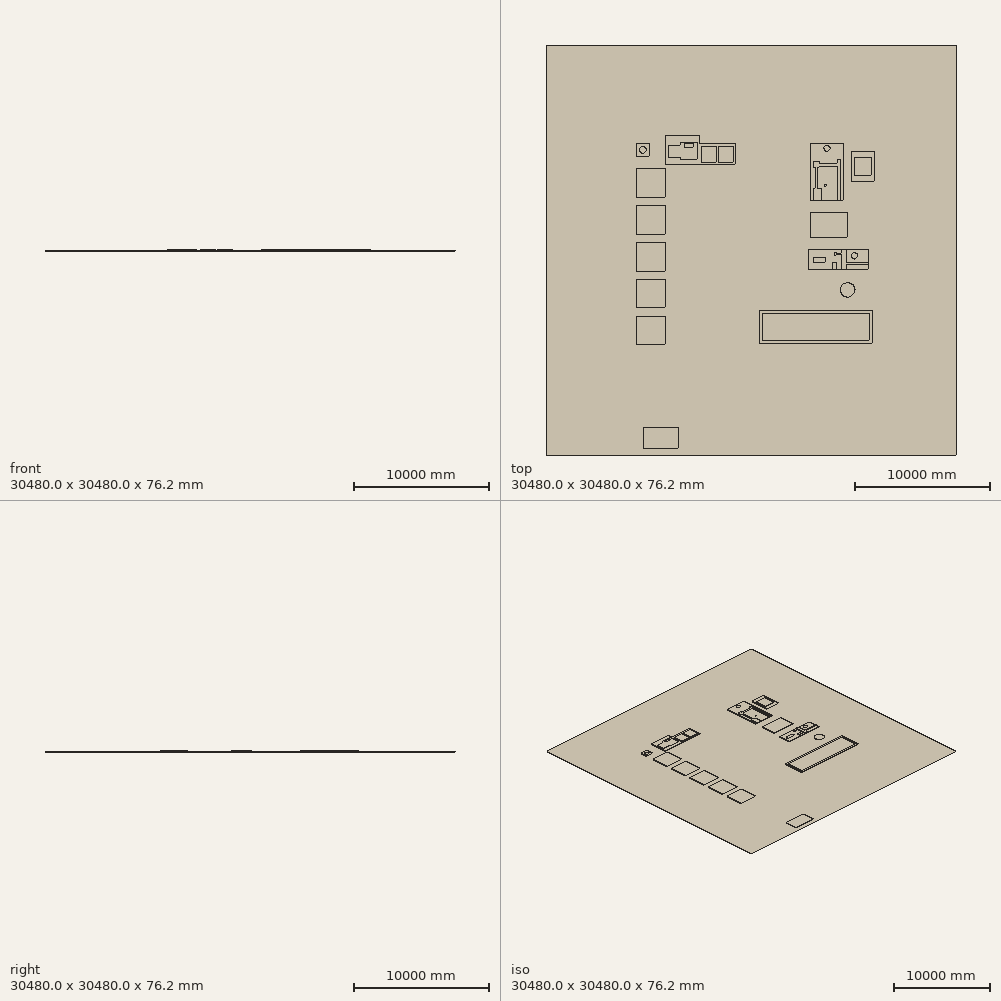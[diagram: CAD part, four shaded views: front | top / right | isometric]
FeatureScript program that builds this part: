
annotation { "Feature Type Name" : "Feature", "Feature Type Description" : "" }
export const myFeature = defineFeature(function(context is Context, id is Id, definition is map)
    precondition{}
    {
        {
            var Q0;
            Q0=qCreatedBy(makeId("Top.planeOp"),FACE);
            var sketch = newSketch(context, id + "F0", { "sketchPlane" : qUnion([Q0])});
            skLineSegment(sketch, "E0.bottom", {"start": v(15240, 15240) * mm, "end": v(-15240, 15240) * mm});
            skLineSegment(sketch, "E0.top", {"start": v(15240, -15240) * mm, "end": v(-15240, -15240) * mm});
            skLineSegment(sketch, "E0.left", {"start": v(15240, 15240) * mm, "end": v(15240, -15240) * mm});
            skLineSegment(sketch, "E0.right", {"start": v(-15240, 15240) * mm, "end": v(-15240, -15240) * mm});
            skPoint(sketch, "E0.middle", {"position": v(0, 0) * mm});
            skSolve(sketch);
        }
        {
            var Q0;
            Q0=qSketchRegion(id+"F0",true);
            extrude(context, id + "F1", {"entities" : qUnion([Q0]), "depth" : 25.4 * mm, "offsetDistance" : 25.4 * mm});
        }
        {
            var Q0;
            Q0=makeQuery(id+"F1.opExtrude","CAP_FACE",FACE,{"disambiguationData":[OSD([sQuery(id+"F0.wireOp",EDGE,"E0.bottom"),sQuery(id+"F0.wireOp",EDGE,"E0.top"),sQuery(id+"F0.wireOp",EDGE,"E0.left"),sQuery(id+"F0.wireOp",EDGE,"E0.right")])],"isStart":false});
            var sketch = newSketch(context, id + "F2", { "sketchPlane" : qUnion([Q0])});
            skLineSegment(sketch, "E1.bottom", {"start": v(-6400.8, 7975.6) * mm, "end": v(-1219.2, 7975.6) * mm});
            skLineSegment(sketch, "E1.top", {"start": v(-6400.8, 6400.8) * mm, "end": v(-1219.2, 6400.8) * mm});
            skLineSegment(sketch, "E1.left", {"start": v(-6400.8, 7975.6) * mm, "end": v(-6400.8, 6400.8) * mm});
            skLineSegment(sketch, "E1.right", {"start": v(-1219.2, 7975.6) * mm, "end": v(-1219.2, 6400.8) * mm});
            skLineSegment(sketch, "E2.bottom", {"start": v(-8534.4, 7924.8) * mm, "end": v(-7620, 7924.8) * mm});
            skLineSegment(sketch, "E2.top", {"start": v(-8534.4, 7010.4) * mm, "end": v(-7620, 7010.4) * mm});
            skLineSegment(sketch, "E2.left", {"start": v(-8534.4, 7924.8) * mm, "end": v(-8534.4, 7010.4) * mm});
            skLineSegment(sketch, "E2.right", {"start": v(-7620, 7924.8) * mm, "end": v(-7620, 7010.4) * mm});
            skCircle(sketch, "E3", {"center": v(-8077.2, 7467.6) * mm, "radius": 254 * mm});
            skLineSegment(sketch, "E4.bottom", {"start": v(4242.66, 50.8) * mm, "end": v(8687.66, 50.8) * mm});
            skLineSegment(sketch, "E4.top", {"start": v(4242.66, -1397) * mm, "end": v(8687.66, -1397) * mm});
            skLineSegment(sketch, "E4.left", {"start": v(4242.66, 50.8) * mm, "end": v(4242.66, -1397) * mm});
            skLineSegment(sketch, "E4.right", {"start": v(8687.66, 50.8) * mm, "end": v(8687.66, -1397) * mm});
            skCircle(sketch, "E5", {"center": v(7163.66, -2934.73) * mm, "radius": 533.4 * mm});
            skLineSegment(sketch, "E6.bottom", {"start": v(610.46, -4458.73) * mm, "end": v(8992.46, -4458.73) * mm});
            skLineSegment(sketch, "E6.top", {"start": v(610.46, -6897.13) * mm, "end": v(8992.46, -6897.13) * mm});
            skLineSegment(sketch, "E6.left", {"start": v(610.46, -4458.73) * mm, "end": v(610.46, -6897.13) * mm});
            skLineSegment(sketch, "E6.right", {"start": v(8992.46, -4458.73) * mm, "end": v(8992.46, -6897.13) * mm});
            skLineSegment(sketch, "E7.bottom", {"start": v(-6400.8, 7975.6) * mm, "end": v(-3860.8, 7975.6) * mm});
            skLineSegment(sketch, "E7.top", {"start": v(-6400.8, 8534.4) * mm, "end": v(-3860.8, 8534.4) * mm});
            skLineSegment(sketch, "E7.left", {"start": v(-6400.8, 7975.6) * mm, "end": v(-6400.8, 8534.4) * mm});
            skLineSegment(sketch, "E7.right", {"start": v(-3860.8, 7975.6) * mm, "end": v(-3860.8, 8534.4) * mm});
            skLineSegment(sketch, "E8.bottom", {"start": v(7442.2, 7366) * mm, "end": v(9144, 7366) * mm});
            skLineSegment(sketch, "E8.top", {"start": v(7442.2, 5105.4) * mm, "end": v(9144, 5105.4) * mm});
            skLineSegment(sketch, "E8.left", {"start": v(7442.2, 7366) * mm, "end": v(7442.2, 5105.4) * mm});
            skLineSegment(sketch, "E8.right", {"start": v(9144, 7366) * mm, "end": v(9144, 5105.4) * mm});
            skLineSegment(sketch, "E9.bottom", {"start": v(4394.2, 7975.6) * mm, "end": v(6832.6, 7975.6) * mm});
            skLineSegment(sketch, "E9.top", {"start": v(4394.2, 3708.4) * mm, "end": v(6832.6, 3708.4) * mm});
            skLineSegment(sketch, "E9.left", {"start": v(4394.2, 7975.6) * mm, "end": v(4394.2, 3708.4) * mm});
            skLineSegment(sketch, "E9.right", {"start": v(6832.6, 7975.6) * mm, "end": v(6832.6, 3708.4) * mm});
            skLineSegment(sketch, "E10.bottom", {"start": v(-8534.4, 3962.4) * mm, "end": v(-8534.4, 6096) * mm});
            skLineSegment(sketch, "E10.top", {"start": v(-6400.8, 3962.4) * mm, "end": v(-6400.8, 6096) * mm});
            skLineSegment(sketch, "E10.left", {"start": v(-8534.4, 3962.4) * mm, "end": v(-6400.8, 3962.4) * mm});
            skLineSegment(sketch, "E10.right", {"start": v(-8534.4, 6096) * mm, "end": v(-6400.8, 6096) * mm});
            skLineSegment(sketch, "E11.bottom", {"start": v(-8534.4, 3352.8) * mm, "end": v(-6400.8, 3352.8) * mm});
            skLineSegment(sketch, "E11.top", {"start": v(-8534.4, 1219.2) * mm, "end": v(-6400.8, 1219.2) * mm});
            skLineSegment(sketch, "E11.left", {"start": v(-8534.4, 3352.8) * mm, "end": v(-8534.4, 1219.2) * mm});
            skLineSegment(sketch, "E11.right", {"start": v(-6400.8, 3352.8) * mm, "end": v(-6400.8, 1219.2) * mm});
            skLineSegment(sketch, "E12.bottom", {"start": v(-8534.4, 609.6) * mm, "end": v(-6400.8, 609.6) * mm});
            skLineSegment(sketch, "E12.top", {"start": v(-8534.4, -1524) * mm, "end": v(-6400.8, -1524) * mm});
            skLineSegment(sketch, "E12.left", {"start": v(-8534.4, 609.6) * mm, "end": v(-8534.4, -1524) * mm});
            skLineSegment(sketch, "E12.right", {"start": v(-6400.8, 609.6) * mm, "end": v(-6400.8, -1524) * mm});
            skLineSegment(sketch, "E13.bottom", {"start": v(-8534.4, -2133.6) * mm, "end": v(-6400.8, -2133.6) * mm});
            skLineSegment(sketch, "E13.top", {"start": v(-8534.4, -4267.2) * mm, "end": v(-6400.8, -4267.2) * mm});
            skLineSegment(sketch, "E13.left", {"start": v(-8534.4, -2133.6) * mm, "end": v(-8534.4, -4267.2) * mm});
            skLineSegment(sketch, "E13.right", {"start": v(-6400.8, -2133.6) * mm, "end": v(-6400.8, -4267.2) * mm});
            skLineSegment(sketch, "E14.bottom", {"start": v(-8534.4, -4876.8) * mm, "end": v(-6400.8, -4876.8) * mm});
            skLineSegment(sketch, "E14.top", {"start": v(-8534.4, -7010.4) * mm, "end": v(-6400.8, -7010.4) * mm});
            skLineSegment(sketch, "E14.left", {"start": v(-8534.4, -4876.8) * mm, "end": v(-8534.4, -7010.4) * mm});
            skLineSegment(sketch, "E14.right", {"start": v(-6400.8, -4876.8) * mm, "end": v(-6400.8, -7010.4) * mm});
            skLineSegment(sketch, "E15.bottom", {"start": v(4395.06, 2794) * mm, "end": v(7138.26, 2794) * mm});
            skLineSegment(sketch, "E15.top", {"start": v(4395.06, 965.2) * mm, "end": v(7138.26, 965.2) * mm});
            skLineSegment(sketch, "E15.left", {"start": v(4395.06, 2794) * mm, "end": v(4395.06, 965.2) * mm});
            skLineSegment(sketch, "E15.right", {"start": v(7138.26, 2794) * mm, "end": v(7138.26, 965.2) * mm});
            skLineSegment(sketch, "E16.bottom", {"start": v(-8062.16, -13190.43) * mm, "end": v(-5457.19, -13190.43) * mm});
            skLineSegment(sketch, "E16.top", {"start": v(-8062.16, -14725.5) * mm, "end": v(-5457.19, -14725.5) * mm});
            skLineSegment(sketch, "E16.left", {"start": v(-8062.16, -13190.43) * mm, "end": v(-8062.16, -14725.5) * mm});
            skLineSegment(sketch, "E16.right", {"start": v(-5457.19, -13190.43) * mm, "end": v(-5457.19, -14725.5) * mm});
            skSolve(sketch);
        }
        {
            var Q0;
            Q0=qSketchRegion(id+"F2",true);
            extrude(context, id + "F3", {"entities" : qUnion([Q0]), "operationType" : NewBodyOperationType.ADD, "depth" : 25.4 * mm, "offsetDistance" : 25.4 * mm});
        }
        {
            var Q0;
            Q0=makeQuery(id+"F3.opExtrude","CAP_FACE",FACE,{"disambiguationData":[OSD([sQuery(id+"F2.wireOp",EDGE,"E1.bottom"),sQuery(id+"F2.wireOp",EDGE,"E1.top"),sQuery(id+"F2.wireOp",EDGE,"E1.left"),sQuery(id+"F2.wireOp",EDGE,"E1.right"),sQuery(id+"F2.wireOp",EDGE,"biDbiMLD-SDf2-hi3V-axfX-EiKsOqyBmbyk.top"),sQuery(id+"F2.wireOp",EDGE,"biDbiMLD-SDf2-hi3V-axfX-EiKsOqyBmbyk.left"),sQuery(id+"F2.wireOp",EDGE,"biDbiMLD-SDf2-hi3V-axfX-EiKsOqyBmbyk.right")])],"isStart":false});
            var sketch = newSketch(context, id + "F4", { "sketchPlane" : qUnion([Q0])});
            skPoint(sketch, "E17.centerSnap0", {"position": v(-1219.2, 7188.2) * mm});
            skLineSegment(sketch, "E18.bottom", {"start": v(4572.86, -508) * mm, "end": v(5538.06, -508) * mm});
            skLineSegment(sketch, "E18.top", {"start": v(4572.86, -889) * mm, "end": v(5538.06, -889) * mm});
            skLineSegment(sketch, "E18.left", {"start": v(4572.86, -508) * mm, "end": v(4572.86, -889) * mm});
            skLineSegment(sketch, "E18.right", {"start": v(5538.06, -508) * mm, "end": v(5538.06, -889) * mm});
            skLineSegment(sketch, "E19.bottom", {"start": v(6147.66, -127) * mm, "end": v(6350.86, -127) * mm});
            skLineSegment(sketch, "E19.top", {"start": v(6147.66, -406.4) * mm, "end": v(6350.86, -406.4) * mm});
            skLineSegment(sketch, "E19.left", {"start": v(6147.66, -127) * mm, "end": v(6147.66, -406.4) * mm});
            skLineSegment(sketch, "E19.right", {"start": v(6350.86, -127) * mm, "end": v(6350.86, -406.4) * mm});
            skLineSegment(sketch, "E20.bottom", {"start": v(6655.66, 50.8) * mm, "end": v(7036.66, 50.8) * mm});
            skLineSegment(sketch, "E20.top", {"start": v(6655.66, -1397) * mm, "end": v(7036.66, -1397) * mm});
            skLineSegment(sketch, "E20.left", {"start": v(6655.66, 50.8) * mm, "end": v(6655.66, -1397) * mm});
            skLineSegment(sketch, "E20.right", {"start": v(7036.66, 50.8) * mm, "end": v(7036.66, -1397) * mm});
            skLineSegment(sketch, "E21.bottom", {"start": v(7036.66, -1041.4) * mm, "end": v(8687.66, -1041.4) * mm});
            skLineSegment(sketch, "E21.top", {"start": v(7036.66, -889) * mm, "end": v(8687.66, -889) * mm});
            skLineSegment(sketch, "E21.left", {"start": v(7036.66, -1041.4) * mm, "end": v(7036.66, -889) * mm});
            skLineSegment(sketch, "E21.right", {"start": v(8687.66, -1041.4) * mm, "end": v(8687.66, -889) * mm});
            skLineSegment(sketch, "E22.bottom", {"start": v(6655.66, -304.8) * mm, "end": v(6350.86, -304.8) * mm});
            skLineSegment(sketch, "E22.top", {"start": v(6655.66, -203.2) * mm, "end": v(6350.86, -203.2) * mm});
            skLineSegment(sketch, "E22.left", {"start": v(6655.66, -304.8) * mm, "end": v(6655.66, -203.2) * mm});
            skLineSegment(sketch, "E22.right", {"start": v(6350.86, -304.8) * mm, "end": v(6350.86, -203.2) * mm});
            skCircle(sketch, "E23", {"center": v(7671.66, -406.4) * mm, "radius": 228.6 * mm});
            skLineSegment(sketch, "E24.bottom", {"start": v(5995.26, -1397) * mm, "end": v(6300.06, -1397) * mm});
            skLineSegment(sketch, "E24.top", {"start": v(5995.26, -914.4) * mm, "end": v(6300.06, -914.4) * mm});
            skLineSegment(sketch, "E24.left", {"start": v(5995.26, -1397) * mm, "end": v(5995.26, -914.4) * mm});
            skLineSegment(sketch, "E24.right", {"start": v(6300.06, -1397) * mm, "end": v(6300.06, -914.4) * mm});
            skLineSegment(sketch, "E25.bottom", {"start": v(-6197.6, 7594.6) * mm, "end": v(-5283.2, 7594.6) * mm});
            skLineSegment(sketch, "E25.top", {"start": v(-6197.6, 7086.6) * mm, "end": v(-5283.2, 7086.6) * mm});
            skLineSegment(sketch, "E25.left", {"start": v(-6197.6, 7594.6) * mm, "end": v(-6197.6, 7086.6) * mm});
            skLineSegment(sketch, "E25.right", {"start": v(-5283.2, 7594.6) * mm, "end": v(-5283.2, 7086.6) * mm});
            skLineSegment(sketch, "E26.bottom", {"start": v(-5283.2, 8051.8) * mm, "end": v(-4013.2, 8051.8) * mm});
            skLineSegment(sketch, "E26.top", {"start": v(-5283.2, 6781.8) * mm, "end": v(-4013.2, 6781.8) * mm});
            skLineSegment(sketch, "E26.left", {"start": v(-5283.2, 8051.8) * mm, "end": v(-5283.2, 6781.8) * mm});
            skLineSegment(sketch, "E26.right", {"start": v(-4013.2, 8051.8) * mm, "end": v(-4013.2, 6781.8) * mm});
            skLineSegment(sketch, "E27.bottom", {"start": v(-4953, 7924.8) * mm, "end": v(-4318, 7924.8) * mm});
            skLineSegment(sketch, "E27.top", {"start": v(-4953, 7620) * mm, "end": v(-4318, 7620) * mm});
            skLineSegment(sketch, "E27.left", {"start": v(-4953, 7924.8) * mm, "end": v(-4953, 7620) * mm});
            skLineSegment(sketch, "E27.right", {"start": v(-4318, 7924.8) * mm, "end": v(-4318, 7620) * mm});
            skLineSegment(sketch, "E28.bottom", {"start": v(-6197.6, 7797.8) * mm, "end": v(-5283.2, 7797.8) * mm});
            skLineSegment(sketch, "E28.top", {"start": v(-6197.6, 6883.4) * mm, "end": v(-5283.2, 6883.4) * mm});
            skLineSegment(sketch, "E28.left", {"start": v(-6197.6, 7797.8) * mm, "end": v(-6197.6, 6883.4) * mm});
            skLineSegment(sketch, "E28.right", {"start": v(-5283.2, 7797.8) * mm, "end": v(-5283.2, 6883.4) * mm});
            skLineSegment(sketch, "E29.bottom", {"start": v(-3733.8, 7721.6) * mm, "end": v(-2590.8, 7721.6) * mm});
            skLineSegment(sketch, "E29.top", {"start": v(-3733.8, 6578.6) * mm, "end": v(-2590.8, 6578.6) * mm});
            skLineSegment(sketch, "E29.left", {"start": v(-3733.8, 7721.6) * mm, "end": v(-3733.8, 6578.6) * mm});
            skLineSegment(sketch, "E29.right", {"start": v(-2590.8, 7721.6) * mm, "end": v(-2590.8, 6578.6) * mm});
            skLineSegment(sketch, "E30.bottom", {"start": v(-2489.2, 7721.6) * mm, "end": v(-1346.2, 7721.6) * mm});
            skLineSegment(sketch, "E30.top", {"start": v(-2489.2, 6578.6) * mm, "end": v(-1346.2, 6578.6) * mm});
            skLineSegment(sketch, "E30.left", {"start": v(-2489.2, 7721.6) * mm, "end": v(-2489.2, 6578.6) * mm});
            skLineSegment(sketch, "E30.right", {"start": v(-1346.2, 7721.6) * mm, "end": v(-1346.2, 6578.6) * mm});
            skLineSegment(sketch, "E31.bottom", {"start": v(7683.5, 6934.2) * mm, "end": v(8902.7, 6934.2) * mm});
            skLineSegment(sketch, "E31.top", {"start": v(7683.5, 5562.6) * mm, "end": v(8902.7, 5562.6) * mm});
            skLineSegment(sketch, "E31.left", {"start": v(7683.5, 6934.2) * mm, "end": v(7683.5, 5562.6) * mm});
            skLineSegment(sketch, "E31.right", {"start": v(8902.7, 6934.2) * mm, "end": v(8902.7, 5562.6) * mm});
            skLineSegment(sketch, "E32.bottom", {"start": v(4607.56, 3708.4) * mm, "end": v(5217.16, 3708.4) * mm});
            skLineSegment(sketch, "E32.top", {"start": v(4607.56, 4622.8) * mm, "end": v(5217.16, 4622.8) * mm});
            skLineSegment(sketch, "E32.left", {"start": v(4607.56, 3708.4) * mm, "end": v(4607.56, 4622.8) * mm});
            skLineSegment(sketch, "E32.right", {"start": v(5217.16, 3708.4) * mm, "end": v(5217.16, 4622.8) * mm});
            skPoint(sketch, "E33.oppositeSnap0", {"position": v(4912.36, 4622.8) * mm});
            skLineSegment(sketch, "E33.bottom", {"start": v(4790.44, 4622.8) * mm, "end": v(4912.36, 4622.8) * mm});
            skLineSegment(sketch, "E33.top", {"start": v(4790.44, 6146.8) * mm, "end": v(4912.36, 6146.8) * mm});
            skLineSegment(sketch, "E33.left", {"start": v(4790.44, 4622.8) * mm, "end": v(4790.44, 6146.8) * mm});
            skLineSegment(sketch, "E33.right", {"start": v(4912.36, 4622.8) * mm, "end": v(4912.36, 6146.8) * mm});
            skLineSegment(sketch, "E34.bottom", {"start": v(4607.56, 6146.8) * mm, "end": v(5064.76, 6146.8) * mm});
            skLineSegment(sketch, "E34.top", {"start": v(4607.56, 6604) * mm, "end": v(5064.76, 6604) * mm});
            skLineSegment(sketch, "E34.left", {"start": v(4607.56, 6146.8) * mm, "end": v(4607.56, 6604) * mm});
            skLineSegment(sketch, "E34.right", {"start": v(5064.76, 6146.8) * mm, "end": v(5064.76, 6604) * mm});
            skLineSegment(sketch, "E35.bottom", {"start": v(6405.88, 6756.4) * mm, "end": v(6619.24, 6756.4) * mm});
            skLineSegment(sketch, "E35.top", {"start": v(6405.88, 3708.4) * mm, "end": v(6619.24, 3708.4) * mm});
            skLineSegment(sketch, "E35.left", {"start": v(6405.88, 6756.4) * mm, "end": v(6405.88, 3708.4) * mm});
            skLineSegment(sketch, "E35.right", {"start": v(6619.24, 6756.4) * mm, "end": v(6619.24, 3708.4) * mm});
            skCircle(sketch, "E36", {"center": v(5613.4, 7594.6) * mm, "radius": 228.6 * mm});
            skLineSegment(sketch, "E37.bottom", {"start": v(5064.76, 6451.6) * mm, "end": v(6405.88, 6451.6) * mm});
            skLineSegment(sketch, "E37.top", {"start": v(5064.76, 6268.72) * mm, "end": v(6405.88, 6268.72) * mm});
            skLineSegment(sketch, "E37.left", {"start": v(5064.76, 6451.6) * mm, "end": v(5064.76, 6268.72) * mm});
            skLineSegment(sketch, "E37.right", {"start": v(6405.88, 6451.6) * mm, "end": v(6405.88, 6268.72) * mm});
            skLineSegment(sketch, "E38.bottom", {"start": v(5445.76, 4927.6) * mm, "end": v(5598.16, 4927.6) * mm});
            skLineSegment(sketch, "E38.top", {"start": v(5445.76, 4775.2) * mm, "end": v(5598.16, 4775.2) * mm});
            skLineSegment(sketch, "E38.left", {"start": v(5445.76, 4927.6) * mm, "end": v(5445.76, 4775.2) * mm});
            skLineSegment(sketch, "E38.right", {"start": v(5598.16, 4927.6) * mm, "end": v(5598.16, 4775.2) * mm});
            skLineSegment(sketch, "E39.bottom", {"start": v(814.68, -4662.95) * mm, "end": v(8788.24, -4662.95) * mm});
            skLineSegment(sketch, "E39.top", {"start": v(814.68, -6692.92) * mm, "end": v(8788.24, -6692.92) * mm});
            skLineSegment(sketch, "E39.left", {"start": v(814.68, -4662.95) * mm, "end": v(814.68, -6692.92) * mm});
            skLineSegment(sketch, "E39.right", {"start": v(8788.24, -4662.95) * mm, "end": v(8788.24, -6692.92) * mm});
            skSolve(sketch);
        }
        {
            var Q0;
            Q0=qSketchRegion(id+"F4",true);
            extrude(context, id + "F5", {"entities" : qUnion([Q0]), "operationType" : NewBodyOperationType.ADD, "depth" : 25.4 * mm, "offsetDistance" : 25.4 * mm});
        }
    });
